# Revit family: KEUCO_34912010800
name_source: partatom
category: Allgemeines Modell
revit_build: Autodesk Revit 2016 (Build: 20150220_1215(x64)
units: mm (PartAtom-declared; Revit-internal decimal feet)

## family parameters
Arbeitsebenenbasiert = Ja
Beim Laden mit Abzugskörper schneiden = Nein
Bemaßung runder Anschluss = Durchmesser verwenden
Gemeinsam genutzt = Nein
Immer vertikal = Nein
Kann Basisbauteil für Bewehrung sein = Nein
Raumberechnungspunkt = Nein
Teiletyp = Normal

## types (6) — shared parameters
Beschreibung = komplett mit Brauseschieber
Hersteller = KEUCO
Serie = Plan
URL = https://www.keuco.com
Vorgabe-Ansicht = 1219 mm
zero-valued in all types: Gewicht

## per-type parameters (varying)
| type | Ausschreibungstext | Material Stange | Stange Material |
| 34912010800 | KEUCO PLAN CARE Brausestange 34912010800
hochglanzverchromte Brausestange 
in ästhetischem, funktionalem und ergonomischem Design, 
komplett mit Brauseschieber,
als Haltegriff bis 115 kg belastbar, 
antistatisch, leicht zu reinigen,
Rohrdurchmesser 33 mm, Rosettendurchmesser 82 mm,
Achsmaß 800 mm, bei einer Gesamthöhe von 882 mm
Ausladung 90 mm, Wandabstand 57 mm,
Die Brausestange wird verdeckt angebracht

Im Lieferumfang enthalten: 
2 x Befestigungs-Set 1 
Art.-Nr. 34990000100 (je 1 x pro Wandbefestigung) 

Weitere Befestigungs-Sets
(je nach Ankergrund/Mauerwerk):
2 x Befestigungs-Set 4 (Art.-Nr. 34990000200) oder
2 x Befestigungs-Set 7 (Art.-Nr. 34993000200) | 880 mm  [stored 2.88714 ft] | Verchromt |
| 34912010900 | KEUCO PLAN CARE Brausestange 34912010900
hochglanzverchromte Brausestange 
in ästhetischem, funktionalem und ergonomischem Design, 
komplett mit Brauseschieber,
als Haltegriff bis 115 kg belastbar, 
antistatisch, leicht zu reinigen,
Rohrdurchmesser 33 mm, Rosettendurchmesser 82 mm,
Achsmaß 900 mm, bei einer Gesamthöhe von 982 mm
Ausladung 90 mm, Wandabstand 57 mm,
Die Brausestange wird verdeckt angebracht

Im Lieferumfang enthalten: 
2 x Befestigungs-Set 1 
Art.-Nr. 34990000100 (je 1 x pro Wandbefestigung) 

Weitere Befestigungs-Sets
(je nach Ankergrund/Mauerwerk):
2 x Befestigungs-Set 4 (Art.-Nr. 34990000200) oder
2 x Befestigungs-Set 7 (Art.-Nr. 34993000200) | 980 mm  [stored 3.21522 ft] | Verchromt |
| 34912011100 | KEUCO PLAN CARE Brausestange 34912011100
hochglanzverchromte Brausestange 
in ästhetischem, funktionalem und ergonomischem Design, 
komplett mit Brauseschieber,
als Haltegriff bis 115 kg belastbar, 
antistatisch, leicht zu reinigen,
Rohrdurchmesser 33 mm, Rosettendurchmesser 82 mm,
Achsmaß 1100 mm, bei einer Gesamthöhe von 1182 mm
Ausladung 90 mm, Wandabstand 57 mm,
Die Brausestange wird verdeckt angebracht

Im Lieferumfang enthalten: 
2 x Befestigungs-Set 1 
Art.-Nr. 34990000100 (je 1 x pro Wandbefestigung) 

Weitere Befestigungs-Sets
(je nach Ankergrund/Mauerwerk):
2 x Befestigungs-Set 4 (Art.-Nr. 34990000200) oder
2 x Befestigungs-Set 7 (Art.-Nr. 34993000200) | 1180 mm  [stored 3.87139 ft] | Verchromt |
| 34912170800 | KEUCO PLAN CARE Brausestange 34912170800
Brausestange 
in Aluminium silber-eloxiert (E6 EV1)/verchromt,
in ästhetischem, funktionalem und ergonomischem Design, 
komplett mit Brauseschieber,
als Haltegriff bis 115 kg belastbar, 
antistatisch, leicht zu reinigen,
Rohrdurchmesser 33 mm, Rosettendurchmesser 82 mm,
Achsmaß 800 mm, bei einer Gesamthöhe von 882 mm
Ausladung 90 mm, Wandabstand 57 mm,
Die Brausestange wird verdeckt angebracht

Im Lieferumfang enthalten: 
2 x Befestigungs-Set 1 
Art.-Nr. 34990000100 (je 1 x pro Wandbefestigung) 

Weitere Befestigungs-Sets
(je nach Ankergrund/Mauerwerk):
2 x Befestigungs-Set 4 (Art.-Nr. 34990000200) oder
2 x Befestigungs-Set 7 (Art.-Nr. 34993000200) | 880 mm  [stored 2.88714 ft] | Aluminium silber-eloxiert (E6 EV1) |
| 34912170900 | KEUCO PLAN CARE Brausestange 34912170900
Brausestange 
in Aluminium silber-eloxiert (E6 EV1)/verchromt,
in ästhetischem, funktionalem und ergonomischem Design, 
komplett mit Brauseschieber,
als Haltegriff bis 115 kg belastbar, 
antistatisch, leicht zu reinigen,
Rohrdurchmesser 33 mm, Rosettendurchmesser 82 mm,
Achsmaß 900 mm, bei einer Gesamthöhe von 982 mm
Ausladung 90 mm, Wandabstand 57 mm,
Die Brausestange wird verdeckt angebracht

Im Lieferumfang enthalten: 
2 x Befestigungs-Set 1 
Art.-Nr. 34990000100 (je 1 x pro Wandbefestigung) 

Weitere Befestigungs-Sets
(je nach Ankergrund/Mauerwerk):
2 x Befestigungs-Set 4 (Art.-Nr. 34990000200) oder
2 x Befestigungs-Set 7 (Art.-Nr. 34993000200) | 980 mm  [stored 3.21522 ft] | Aluminium silber-eloxiert (E6 EV1) |
| 34912171100 | KEUCO PLAN CARE Brausestange 34912171100
Brausestange 
in Aluminium silber-eloxiert (E6 EV1)/verchromt,
in ästhetischem, funktionalem und ergonomischem Design, 
komplett mit Brauseschieber,
als Haltegriff bis 115 kg belastbar, 
antistatisch, leicht zu reinigen,
Rohrdurchmesser 33 mm, Rosettendurchmesser 82 mm,
Achsmaß 1100 mm, bei einer Gesamthöhe von 1182 mm
Ausladung 90 mm, Wandabstand 57 mm,
Die Brausestange wird verdeckt angebracht

Im Lieferumfang enthalten: 
2 x Befestigungs-Set 1 
Art.-Nr. 34990000100 (je 1 x pro Wandbefestigung) 

Weitere Befestigungs-Sets
(je nach Ankergrund/Mauerwerk):
2 x Befestigungs-Set 4 (Art.-Nr. 34990000200) oder
2 x Befestigungs-Set 7 (Art.-Nr. 34993000200) | 1180 mm  [stored 3.87139 ft] | Verchromt |

note: column(s) folded — value = type name in every type: Artikelnummer

note: [stored X ft] marks values corroborated as IEEE doubles in the binary element streams (Revit-internal decimal feet)

## geometry (parser evidence)
native form markers: Sweep x3
no freeform markers — native parametric forms only
